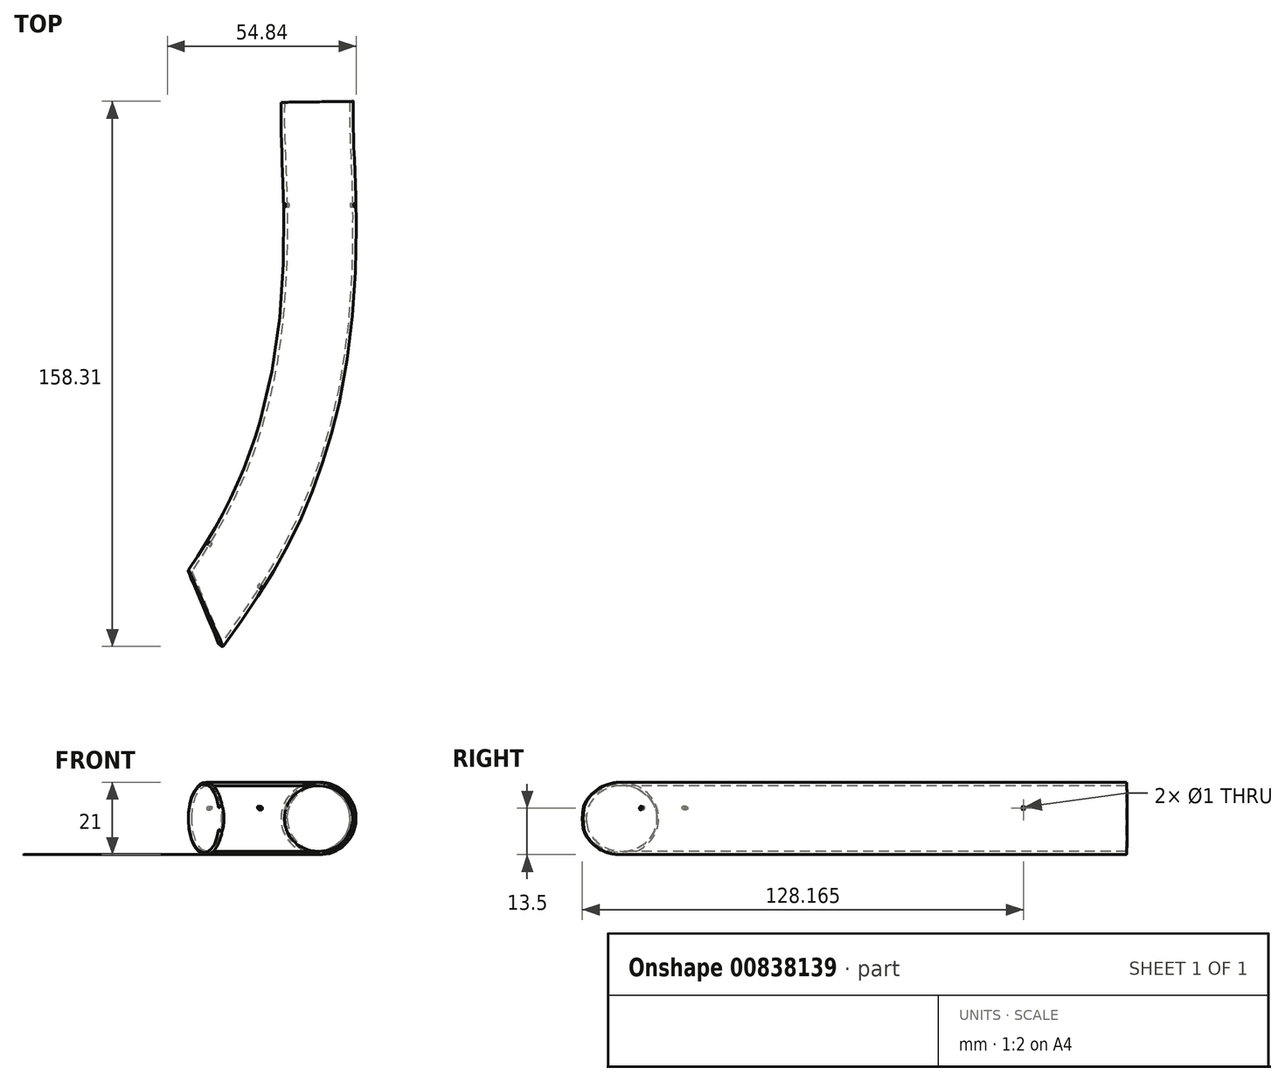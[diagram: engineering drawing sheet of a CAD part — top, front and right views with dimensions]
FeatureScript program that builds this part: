
annotation { "Feature Type Name" : "Feature", "Feature Type Description" : "" }
export const myFeature = defineFeature(function(context is Context, id is Id, definition is map)
    precondition{}
    {
        {
            var Q0;
            Q0=qCreatedBy(makeId("Top.planeOp"),FACE);
            var sketch = newSketch(context, id + "F0", { "sketchPlane" : qUnion([Q0])});
            skLineSegment(sketch, "E0", {"start": v(-2.54, 75.26) * mm, "end": v(-1.95, 58.9) * mm});
            skLineSegment(sketch, "E1", {"start": v(-1.93, 58.9) * mm, "end": v(-1.77, 42.71) * mm});
            skLineSegment(sketch, "E2", {"start": v(-1.64, 42.7) * mm, "end": v(-3.47, 29.3) * mm});
            skLineSegment(sketch, "E3", {"start": v(-3.47, 29.3) * mm, "end": v(-6.55, 16.19) * mm});
            skLineSegment(sketch, "E4", {"start": v(-6.55, 16.19) * mm, "end": v(-12.57, -6.64) * mm});
            skLineSegment(sketch, "E5", {"start": v(-12.57, -6.64) * mm, "end": v(-19.36, -23.76) * mm});
            skLineSegment(sketch, "E6", {"start": v(-19.36, -23.76) * mm, "end": v(-25.52, -35.02) * mm});
            skLineSegment(sketch, "E7", {"start": v(-25.52, -35.02) * mm, "end": v(-27.38, -38.26) * mm});
            skLineSegment(sketch, "E8", {"start": v(-27.38, -38.26) * mm, "end": v(-30.77, -39.34) * mm});
            skLineSegment(sketch, "E9", {"start": v(-30.77, -39.34) * mm, "end": v(-32.93, -42.58) * mm});
            skLineSegment(sketch, "E10", {"start": v(-32.93, -42.58) * mm, "end": v(-31.85, -47.2) * mm});
            skLineSegment(sketch, "E11", {"start": v(-31.85, -47.2) * mm, "end": v(-30.15, -54.76) * mm});
            skLineSegment(sketch, "E12", {"start": v(-30.15, -54.76) * mm, "end": v(-29.07, -65.7) * mm});
            skLineSegment(sketch, "E13", {"start": v(-29.07, -65.7) * mm, "end": v(-27.84, -73.27) * mm});
            skLineSegment(sketch, "E14", {"start": v(-27.84, -73.27) * mm, "end": v(-23.52, -78.2) * mm});
            skLineSegment(sketch, "E15", {"start": v(-23.52, -78.2) * mm, "end": v(-17.04, -80.52) * mm});
            skLineSegment(sketch, "E16", {"start": v(-17.04, -80.52) * mm, "end": v(-10.72, -79.9) * mm});
            skLineSegment(sketch, "E17", {"start": v(-10.72, -79.9) * mm, "end": v(-6.86, -73.73) * mm});
            skLineSegment(sketch, "E18", {"start": v(-6.86, -73.73) * mm, "end": v(-2.7, -66.48) * mm});
            skLineSegment(sketch, "E19", {"start": v(-2.7, -66.48) * mm, "end": v(3.32, -56.76) * mm});
            skLineSegment(sketch, "E20", {"start": v(3.32, -56.76) * mm, "end": v(9.18, -46.12) * mm});
            skLineSegment(sketch, "E21", {"start": v(9.18, -46.12) * mm, "end": v(14.27, -36.56) * mm});
            skLineSegment(sketch, "E22", {"start": v(14.27, -36.56) * mm, "end": v(19.05, -26.54) * mm});
            skLineSegment(sketch, "E23", {"start": v(19.05, -26.54) * mm, "end": v(24.3, -14.81) * mm});
            skLineSegment(sketch, "E24", {"start": v(24.3, -14.81) * mm, "end": v(27.38, -2.63) * mm});
            skLineSegment(sketch, "E25", {"start": v(27.38, -2.63) * mm, "end": v(30.46, 8.32) * mm});
            skLineSegment(sketch, "E26", {"start": v(30.46, 8.32) * mm, "end": v(32.93, 22.5) * mm});
            skLineSegment(sketch, "E27", {"start": v(32.9, 22.5) * mm, "end": v(33.02, 37.46) * mm});
            skLineSegment(sketch, "E28", {"start": v(33.06, 37.56) * mm, "end": v(32.5, 48.6) * mm});
            skLineSegment(sketch, "E29", {"start": v(32.51, 48.62) * mm, "end": v(32.86, 58.4) * mm});
            skLineSegment(sketch, "E30", {"start": v(32.93, 58.5) * mm, "end": v(32.46, 70.78) * mm});
            skLineSegment(sketch, "E31", {"start": v(32.46, 70.78) * mm, "end": v(32.46, 75.72) * mm});
            skLineSegment(sketch, "E32", {"start": v(-2.8, 92.92) * mm, "end": v(32.2, 92.92) * mm});
            skLineSegment(sketch, "E33", {"start": v(-2.8, 92.92) * mm, "end": v(-2.54, 75.26) * mm});
            skLineSegment(sketch, "E34", {"start": v(32.2, 92.92) * mm, "end": v(32.46, 75.72) * mm});
            skLineSegment(sketch, "E35.0", {"start": v(6.35, 75.48) * mm, "end": v(6.98, 58.4) * mm});
            skLineSegment(sketch, "E35.1", {"start": v(6.23, 84.02) * mm, "end": v(6.35, 75.48) * mm});
            skLineSegment(sketch, "E35.2", {"start": v(6.23, 84.02) * mm, "end": v(23.44, 84.02) * mm});
            skLineSegment(sketch, "E35.3", {"start": v(23.44, 84.02) * mm, "end": v(23.56, 75.65) * mm});
            skLineSegment(sketch, "E35.4", {"start": v(23.56, 70.61) * mm, "end": v(23.56, 75.65) * mm});
            skLineSegment(sketch, "E35.5", {"start": v(23.99, 59.35) * mm, "end": v(23.56, 70.61) * mm});
            skLineSegment(sketch, "E35.6", {"start": v(23.6, 48.3) * mm, "end": v(23.99, 59.35) * mm});
            skLineSegment(sketch, "E35.7", {"start": v(24.12, 38.12) * mm, "end": v(23.6, 48.3) * mm});
            skLineSegment(sketch, "E35.8", {"start": v(24, 23.1) * mm, "end": v(24.12, 38.12) * mm});
            skLineSegment(sketch, "E35.9", {"start": v(-20.24, -64.55) * mm, "end": v(-19.46, -69.32) * mm});
            skLineSegment(sketch, "E35.10", {"start": v(-21.35, -53.34) * mm, "end": v(-20.24, -64.55) * mm});
            skLineSegment(sketch, "E35.11", {"start": v(-22.95, -46.19) * mm, "end": v(-21.35, -53.34) * mm});
            skLineSegment(sketch, "E35.12", {"start": v(-21.37, -45.69) * mm, "end": v(-22.95, -46.19) * mm});
            skLineSegment(sketch, "E35.13", {"start": v(-17.76, -39.36) * mm, "end": v(-21.37, -45.69) * mm});
            skLineSegment(sketch, "E35.14", {"start": v(-11.29, -27.55) * mm, "end": v(-17.76, -39.36) * mm});
            skLineSegment(sketch, "E35.15", {"start": v(7.14, 41.2) * mm, "end": v(5.3, 27.67) * mm});
            skLineSegment(sketch, "E35.16", {"start": v(5.3, 27.67) * mm, "end": v(2.08, 14.03) * mm});
            skLineSegment(sketch, "E35.17", {"start": v(2.08, 14.03) * mm, "end": v(-4.1, -9.42) * mm});
            skLineSegment(sketch, "E35.18", {"start": v(-4.1, -9.42) * mm, "end": v(-11.29, -27.55) * mm});
            skLineSegment(sketch, "E35.19", {"start": v(-19.46, -69.32) * mm, "end": v(-18.35, -70.6) * mm});
            skLineSegment(sketch, "E35.20", {"start": v(-18.35, -70.6) * mm, "end": v(-15.94, -71.46) * mm});
            skLineSegment(sketch, "E35.21", {"start": v(-15.94, -71.46) * mm, "end": v(-14.5, -69.15) * mm});
            skLineSegment(sketch, "E35.22", {"start": v(-14.5, -69.15) * mm, "end": v(-10.34, -61.92) * mm});
            skLineSegment(sketch, "E35.23", {"start": v(-10.34, -61.92) * mm, "end": v(-4.37, -52.27) * mm});
            skLineSegment(sketch, "E35.24", {"start": v(-4.37, -52.27) * mm, "end": v(1.35, -41.88) * mm});
            skLineSegment(sketch, "E35.25", {"start": v(1.35, -41.88) * mm, "end": v(6.32, -32.55) * mm});
            skLineSegment(sketch, "E35.26", {"start": v(6.32, -32.55) * mm, "end": v(10.97, -22.8) * mm});
            skLineSegment(sketch, "E35.27", {"start": v(10.97, -22.8) * mm, "end": v(15.85, -11.88) * mm});
            skLineSegment(sketch, "E35.28", {"start": v(6.98, 58.4) * mm, "end": v(7.14, 41.2) * mm});
            skLineSegment(sketch, "E35.29", {"start": v(15.85, -11.88) * mm, "end": v(18.78, -0.33) * mm});
            skLineSegment(sketch, "E35.30", {"start": v(18.78, -0.33) * mm, "end": v(21.77, 10.3) * mm});
            skLineSegment(sketch, "E35.31", {"start": v(21.77, 10.3) * mm, "end": v(24, 23.1) * mm});
            skLineSegment(sketch, "E36", {"start": v(-11.29, -27.55) * mm, "end": v(6.32, -32.55) * mm, "construction": true});
            skLineSegment(sketch, "E37", {"start": v(-4.1, -9.42) * mm, "end": v(15.85, -11.88) * mm, "construction": true});
            skLineSegment(sketch, "E38", {"start": v(2.08, 14.03) * mm, "end": v(21.77, 10.3) * mm, "construction": true});
            skLineSegment(sketch, "E39", {"start": v(5.3, 27.67) * mm, "end": v(24, 23.1) * mm, "construction": true});
            skLineSegment(sketch, "E40", {"start": v(7.14, 41.2) * mm, "end": v(24.12, 38.12) * mm, "construction": true});
            skLineSegment(sketch, "E41", {"start": v(6.98, 58.4) * mm, "end": v(23.99, 59.35) * mm, "construction": true});
            skLineSegment(sketch, "E42", {"start": v(6.35, 75.48) * mm, "end": v(23.56, 75.65) * mm, "construction": true});
            skPoint(sketch, "E43.1.internal.snap0", {"position": v(14.84, 84.02) * mm});
            skPoint(sketch, "E43.2.internal.snap0", {"position": v(14.84, 84.02) * mm});
            skPoint(sketch, "E43.3.internal.snap0", {"position": v(14.84, 84.02) * mm});
            skPoint(sketch, "E43.4.internal.snap0", {"position": v(14.84, 84.02) * mm});
            skLineSegment(sketch, "E44", {"start": v(6.23, 84.02) * mm, "end": v(6.1, 92.92) * mm});
            skLineSegment(sketch, "E45", {"start": v(23.44, 84.02) * mm, "end": v(23.32, 92.92) * mm});
            skPoint(sketch, "E46.3.internal.snap0", {"position": v(15.63, 39.65) * mm});
            skFitSpline(sketch, "E46", {"points": [v(-20.8, -58.95) * mm, v(-2.48, -30.05) * mm, v(11.93, 12.16) * mm, v(15.63, 58.89) * mm, v(14.84, 84.02) * mm, v(14.84, 92.92) * mm], "startDerivative": vector(89.84, 127.33) * mm, "endDerivative": vector(1.3, 72.83) * mm});
            skSolve(sketch);
        }
        {
            var Q0;
            Q0=sQuery(id+"F0.wireOp",EDGE,"E32");
            cPoint(context, id + "F1", {"entities" : qUnion([Q0]), "parameter" : 0.5});
        }
        {
            var Q0;
            Q0=sQuery(id+"F0.wireOp",EDGE,"E45");
            var Q1;
            Q1 = qCreatedBy(id + "F1" ,VERTEX);
            cPlane(context, id + "F2", {"entities" : qUnion([Q0, Q1]), "cplaneType" : CPlaneType.LINE_POINT, "offset" : 25 * mm, "width" : 150 * mm, "height" : 150 * mm});
        }
        {
            var Q0;
            Q0=qCreatedBy(id+"F2.planeOp",FACE);
            var sketch = newSketch(context, id + "F3", { "sketchPlane" : qUnion([Q0])});
            skCircle(sketch, "E47", {"center": v(-16, 0) * mm, "radius": 9.5 * mm});
            skSolve(sketch);
        }
        {
            var Q0;
            Q0=makeQuery(id+"F3.imprint","IMPRINT",FACE,{"disambiguationData":[TD([[makeQuery(id+"F3.imprint","IMPRINT",EDGE,{"derivedFrom":sQuery(id+"F3.wireOp",EDGE,"E47")}),1.0]])]});
            var Q1;
            Q1=sQuery(id+"F0.wireOp",EDGE,"E46");
            sweep(context, id + "F4", {"profiles" : qUnion([Q0]), "path" : qUnion([Q1])});
        }
        {
            var Q0;
            {var subQ4=sQuery(id+"F0.wireOp",EDGE,"E35.3");Q0=makeQuery(id+"F0.imprint","IMPRINT",FACE,{"disambiguationData":[TD([[makeQuery(id+"F0.imprint","IMPRINT",EDGE,{"derivedFrom":subQ4}),-1.0]])]});}
            var sketch = newSketch(context, id + "F5", { "sketchPlane" : qUnion([Q0])});
            skLineSegment(sketch, "E48", {"start": v(-13, -64.11) * mm, "end": v(-23.42, -39.4) * mm});
            skLineSegment(sketch, "E49", {"start": v(-23.42, -39.4) * mm, "end": v(-35.7, -52.6) * mm});
            skLineSegment(sketch, "E50", {"start": v(-35.7, -52.6) * mm, "end": v(-13, -64.11) * mm});
            skSolve(sketch);
        }
        {
            var Q0;
            {var subQ1=sQuery(id+"F5.wireOp",EDGE,"E49");Q0=makeQuery(id+"F5.imprint","IMPRINT",FACE,{"disambiguationData":[TD([[makeQuery(id+"F5.imprint","IMPRINT",EDGE,{"derivedFrom":subQ1}),1.0]])]});}
            var Q1;
            {var subQ0=sQuery(id+"F5.wireOp",EDGE,"E50");var subQ1=sQuery(id+"F5.wireOp",EDGE,"E48");var subQ2=makeQuery(id+"F5.imprint","INTERSECT",VERTEX,{"derivedFrom":[subQ1,subQ0]});Q1=makeQuery(id+"F5.imprint","IMPRINT",FACE,{"disambiguationData":[TD([[makeQuery(id+"F5.imprint","IMPRINT",EDGE,{"disambiguationData":[TD([[subQ2,-1.0]])],"derivedFrom":subQ1}),1.0]])]});}
            extrude(context, id + "F6", {"entities" : qUnion([Q0, Q1]), "operationType" : NewBodyOperationType.REMOVE, "endBound" : BoundingType.SYMMETRIC, "depth" : 25 * mm, "offsetDistance" : 25 * mm});
        }
        {
            var Q0;
            Q0=makeQuery(id+"F4.opSweep","CAP_FACE",FACE,{"disambiguationData":[OSD([sQuery(id+"F0.wireOp",VERTEX,"8cab86fd-680f-44b3-af3a-94a840ba0b8c.end"),sQuery(id+"F3.wireOp",EDGE,"E47")])],"isStart":true});
            var Q1;
            Q1=makeQuery(id+"F4.opSweep","SWEPT_BODY",BODY,{"disambiguationData":[OSD([sQuery(id+"F0.wireOp",EDGE,"8cab86fd-680f-44b3-af3a-94a840ba0b8c"),sQuery(id+"F3.wireOp",EDGE,"E47")])]});
            shell(context, id + "F7", {"entities" : qUnion([Q0]), "parts" : qUnion([Q1]), "thickness" : 1 * mm, "oppositeDirection" : true});
        }
        {
            var Q0;
            Q0=makeQuery(id+"F6.boolean.opBoolean","INTERSECT",EDGE,{"derivedFrom":[makeQuery(id+"F4.opSweep","SWEPT_FACE",FACE,{"disambiguationData":[OSD([sQuery(id+"F0.wireOp",EDGE,"E46"),sQuery(id+"F3.wireOp",EDGE,"E47")])]}),makeQuery(id+"F6.opExtrude","SWEPT_FACE",FACE,{"disambiguationData":[OSD([sQuery(id+"F5.wireOp",EDGE,"E48")])]})]});
            var Q1;
            Q1=makeQuery(id+"F4.opSweep","CAP_EDGE",EDGE,{"disambiguationData":[OSD([sQuery(id+"F0.wireOp",VERTEX,"E46.start"),sQuery(id+"F3.wireOp",EDGE,"E47")])],"isStart":false});
            fillet(context, id + "F8", {"entities" : qUnion([Q0, Q1]), "radius" : 0.6 * mm, "tangentPropagation" : true, "allowEdgeOverflow" : false});
        }
        {
            var Q0;
            Q0=makeQuery(id+"F6.boolean.opBoolean","INTERSECT",EDGE,{"derivedFrom":[makeQuery(id+"F4.opSweep","CAP_FACE",FACE,{"disambiguationData":[OSD([sQuery(id+"F0.wireOp",VERTEX,"E46.start"),sQuery(id+"F3.wireOp",EDGE,"E47")])],"isStart":false}),makeQuery(id+"F6.opExtrude","SWEPT_FACE",FACE,{"disambiguationData":[OSD([sQuery(id+"F5.wireOp",EDGE,"E48")])]})]});
            fillet(context, id + "F9", {"entities" : qUnion([Q0]), "radius" : 0.4 * mm, "tangentPropagation" : true, "allowEdgeOverflow" : false});
        }
        {
            var Q0;
            Q0=qCreatedBy(makeId("Top.planeOp"),FACE);
            cPlane(context, id + "F10", {"entities" : qUnion([Q0]), "cplaneType" : CPlaneType.OFFSET, "offset" : 3 * mm, "width" : 150 * mm, "height" : 150 * mm});
        }
        {
            var Q0;
            Q0=qCreatedBy(id+"F10.planeOp",FACE);
            var sketch = newSketch(context, id + "F11", { "sketchPlane" : qUnion([Q0])});
            skLineSegment(sketch, "E51", {"start": v(-13.49, 62.92) * mm, "end": v(46.2, 62.92) * mm});
            skLineSegment(sketch, "E52", {"start": v(-32.1, -22.27) * mm, "end": v(14.89, -62) * mm});
            skSolve(sketch);
        }
        {
            var Q0;
            Q0=sQuery(id+"F11.wireOp",EDGE,"E51");
            var Q1;
            Q1=sQuery(id+"F0.wireOp",VERTEX,"E29.end");
            cPlane(context, id + "F12", {"entities" : qUnion([Q0, Q1]), "cplaneType" : CPlaneType.LINE_POINT, "offset" : 25 * mm, "width" : 150 * mm, "height" : 150 * mm});
        }
        {
            var Q0;
            Q0=qCreatedBy(id+"F12.planeOp",FACE);
            var sketch = newSketch(context, id + "F13", { "sketchPlane" : qUnion([Q0])});
            skCircle(sketch, "E53", {"center": v(62.92, 3) * mm, "radius": 0.5 * mm});
            skSolve(sketch);
        }
        {
            var Q0;
            Q0=makeQuery(id+"F13.imprint","IMPRINT",FACE,{"disambiguationData":[TD([[makeQuery(id+"F13.imprint","IMPRINT",EDGE,{"derivedFrom":sQuery(id+"F13.wireOp",EDGE,"E53")}),1.0]])]});
            extrude(context, id + "F14", {"entities" : qUnion([Q0]), "operationType" : NewBodyOperationType.REMOVE, "endBound" : BoundingType.THROUGH_ALL, "oppositeDirection" : true, "depth" : 25 * mm, "offsetDistance" : 25 * mm});
        }
        {
            var Q0;
            Q0=sQuery(id+"F11.wireOp",EDGE,"E52");
            var Q1;
            {var subQ0=sQuery(id+"F3.wireOp",EDGE,"E47");var subQ1=sQuery(id+"F0.wireOp",EDGE,"E46");var subQ2=makeQuery(id+"F4.opSweep","SWEPT_FACE",FACE,{"disambiguationData":[OSD([subQ1,subQ0])]});var subQ3=sQuery(id+"F5.wireOp",EDGE,"E48");var subQ4=sQuery(id+"F0.wireOp",VERTEX,"E46.start");Q1=makeQuery(id+"F9.opFillet","BLEND_VERTEX",VERTEX,{"blendedFrom":[makeQuery(id+"F8.opFillet","BLEND_EDGE",EDGE,{"disambiguationData":[OD(1.0)],"blendedFrom":[makeQuery(id+"F4.opSweep","CAP_EDGE",EDGE,{"disambiguationData":[OSD([subQ4,subQ0])],"isStart":false}),makeQuery(id+"F6.boolean.opBoolean","INTERSECT",EDGE,{"derivedFrom":[subQ2,makeQuery(id+"F6.opExtrude","SWEPT_FACE",FACE,{"disambiguationData":[OSD([subQ3])]})]})],"blendedInto":[]}),makeQuery(id+"F8.opFillet","BLEND_FACE",FACE,{"disambiguationData":[OSD([subQ4,subQ0])]}),makeQuery(id+"F8.opFillet","BLEND_FACE",FACE,{"disambiguationData":[OSD([subQ1,subQ0,subQ3])]}),subQ2],"blendedInto":[makeQuery(id+"F8.opFillet","BLEND_FACE",FACE,{"disambiguationData":[OSD([subQ4,subQ0])]}),makeQuery(id+"F8.opFillet","BLEND_FACE",FACE,{"disambiguationData":[OSD([subQ1,subQ0,subQ3])]}),subQ2]});}
            cPlane(context, id + "F15", {"entities" : qUnion([Q0, Q1]), "cplaneType" : CPlaneType.LINE_POINT, "offset" : 25 * mm, "width" : 150 * mm, "height" : 150 * mm});
        }
        {
            var Q0;
            Q0=qCreatedBy(id+"F15.planeOp",FACE);
            var sketch = newSketch(context, id + "F16", { "sketchPlane" : qUnion([Q0])});
            skCircle(sketch, "E54", {"center": v(-37.8, 3.05) * mm, "radius": 0.5 * mm});
            skSolve(sketch);
        }
        {
            var Q0;
            Q0=makeQuery(id+"F16.imprint","IMPRINT",FACE,{"disambiguationData":[TD([[makeQuery(id+"F16.imprint","IMPRINT",EDGE,{"derivedFrom":sQuery(id+"F16.wireOp",EDGE,"E54")}),1.0]])]});
            extrude(context, id + "F17", {"entities" : qUnion([Q0]), "operationType" : NewBodyOperationType.REMOVE, "endBound" : BoundingType.THROUGH_ALL, "oppositeDirection" : true, "depth" : 25 * mm, "offsetDistance" : 25 * mm});
        }
    });
